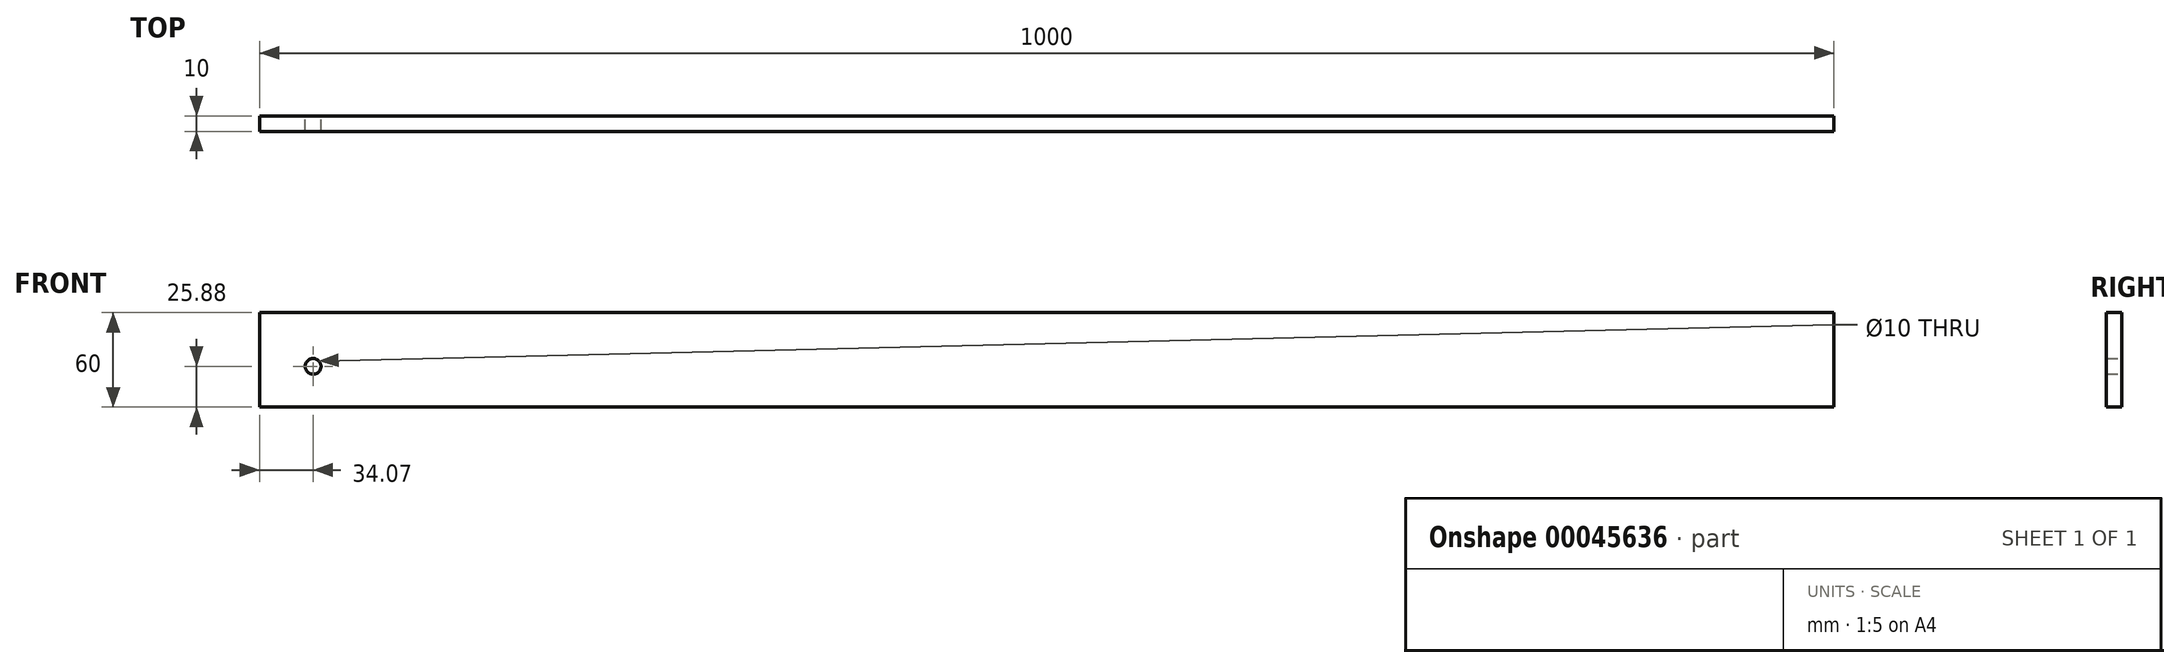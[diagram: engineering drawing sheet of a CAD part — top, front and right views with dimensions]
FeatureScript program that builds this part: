
annotation { "Feature Type Name" : "Feature", "Feature Type Description" : "" }
export const myFeature = defineFeature(function(context is Context, id is Id, definition is map)
    precondition{}
    {
        {
            var Q0;
            Q0=qCreatedBy(makeId("Front.planeOp"),FACE);
            var sketch = newSketch(context, id + "F0", { "sketchPlane" : qUnion([Q0])});
            skLineSegment(sketch, "E0.bottom", {"start": v(-96.26, -25.88) * mm, "end": v(903.74, -25.88) * mm});
            skLineSegment(sketch, "E0.top", {"start": v(-96.26, 34.12) * mm, "end": v(903.74, 34.12) * mm});
            skLineSegment(sketch, "E0.left", {"start": v(-96.26, -25.88) * mm, "end": v(-96.26, 34.12) * mm});
            skLineSegment(sketch, "E0.right", {"start": v(903.74, -25.88) * mm, "end": v(903.74, 34.12) * mm});
            skCircle(sketch, "E1", {"center": v(-62.19, 0) * mm, "radius": 5 * mm});
            skSolve(sketch);
        }
        {
            var Q0;
            Q0=makeQuery(id+"F0.imprint","IMPRINT",FACE,{"disambiguationData":[TD([[makeQuery(id+"F0.imprint","IMPRINT",EDGE,{"derivedFrom":sQuery(id+"F0.wireOp",EDGE,"E0.bottom")}),1.0]])]});
            extrude(context, id + "F1", {"entities" : qUnion([Q0]), "depth" : 10 * mm});
        }
    });
